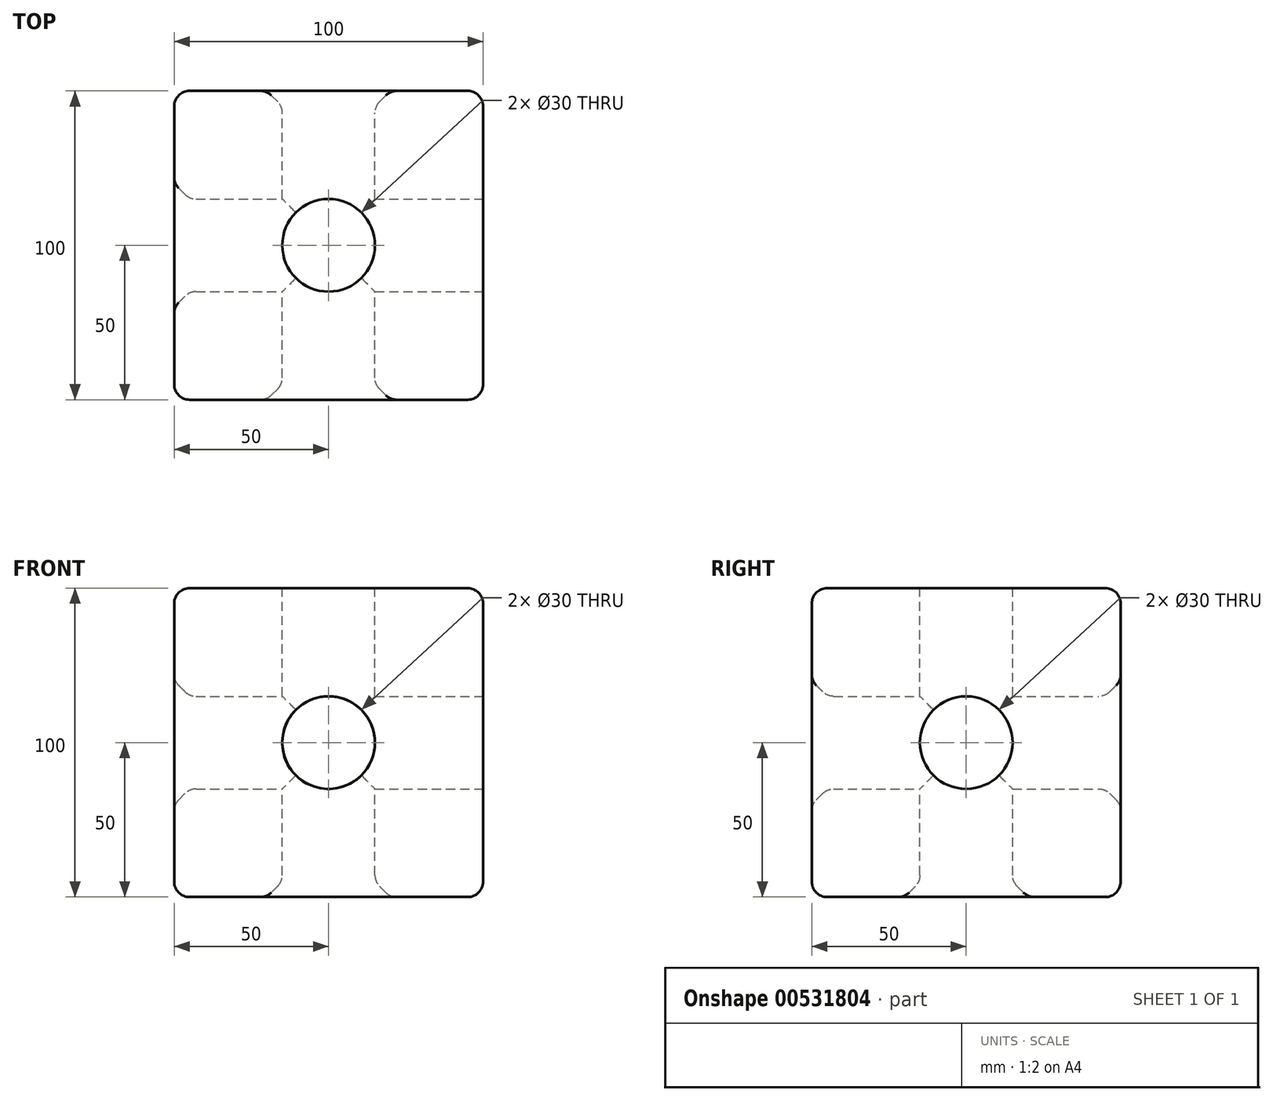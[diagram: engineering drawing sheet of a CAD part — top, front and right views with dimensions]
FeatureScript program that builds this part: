
annotation { "Feature Type Name" : "Feature", "Feature Type Description" : "" }
export const myFeature = defineFeature(function(context is Context, id is Id, definition is map)
    precondition{}
    {
        {
            var Q0;
            Q0=qCreatedBy(makeId("Front.planeOp"),FACE);
            var sketch = newSketch(context, id + "F0", { "sketchPlane" : qUnion([Q0])});
            skLineSegment(sketch, "E0.bottom", {"start": v(-50, 50) * mm, "end": v(50, 50) * mm});
            skLineSegment(sketch, "E0.top", {"start": v(-50, -50) * mm, "end": v(50, -50) * mm});
            skLineSegment(sketch, "E0.left", {"start": v(-50, 50) * mm, "end": v(-50, -50) * mm});
            skLineSegment(sketch, "E0.right", {"start": v(50, 50) * mm, "end": v(50, -50) * mm});
            skCircle(sketch, "E1", {"center": v(0, 0) * mm, "radius": 15 * mm});
            skSolve(sketch);
        }
        {
            var Q0;
            Q0=makeQuery(id+"F0.imprint","IMPRINT",FACE,{"disambiguationData":[TD([[makeQuery(id+"F0.imprint","IMPRINT",EDGE,{"derivedFrom":sQuery(id+"F0.wireOp",EDGE,"E0.bottom")}),-1.0]])]});
            extrude(context, id + "F1", {"entities" : qUnion([Q0]), "endBound" : BoundingType.SYMMETRIC, "depth" : 100 * mm, "offsetDistance" : 25 * mm});
        }
        {
            var Q0;
            Q0=makeQuery(id+"F1.opExtrude","SWEPT_FACE",FACE,{"disambiguationData":[OSD([sQuery(id+"F0.wireOp",EDGE,"E0.bottom")])]});
            var sketch = newSketch(context, id + "F2", { "sketchPlane" : qUnion([Q0])});
            skCircle(sketch, "E2", {"center": v(0, 0) * mm, "radius": 15 * mm});
            skSolve(sketch);
        }
        {
            var Q0;
            Q0 = qSketchRegion(id + "F2", true);
            extrude(context, id + "F3", {"entities" : qUnion([Q0]), "operationType" : NewBodyOperationType.REMOVE, "endBound" : BoundingType.THROUGH_ALL, "oppositeDirection" : true, "depth" : 25 * mm, "offsetDistance" : 25 * mm});
        }
        {
            var Q0;
            Q0=makeQuery(id+"F1.opExtrude","SWEPT_FACE",FACE,{"disambiguationData":[OSD([sQuery(id+"F0.wireOp",EDGE,"E0.right")])]});
            var sketch = newSketch(context, id + "F4", { "sketchPlane" : qUnion([Q0])});
            skCircle(sketch, "E3", {"center": v(0, 0) * mm, "radius": 15 * mm});
            skSolve(sketch);
        }
        {
            var Q0;
            Q0 = qSketchRegion(id + "F4", true);
            extrude(context, id + "F5", {"entities" : qUnion([Q0]), "operationType" : NewBodyOperationType.REMOVE, "endBound" : BoundingType.THROUGH_ALL, "oppositeDirection" : true, "depth" : 25 * mm, "offsetDistance" : 25 * mm});
        }
        {
            var Q0;
            Q0=makeQuery(id+"F1.opExtrude","CAP_EDGE",EDGE,{"disambiguationData":[OSD([sQuery(id+"F0.wireOp",EDGE,"E0.bottom")])],"isStart":true});
            var Q1;
            Q1=makeQuery(id+"F1.opExtrude","SWEPT_EDGE",EDGE,{"disambiguationData":[OSD([sQuery(id+"F0.wireOp",EDGE,"E0.bottom"),sQuery(id+"F0.wireOp",EDGE,"E0.left")])]});
            var Q2;
            Q2=makeQuery(id+"F1.opExtrude","CAP_EDGE",EDGE,{"disambiguationData":[OSD([sQuery(id+"F0.wireOp",EDGE,"E0.bottom")])],"isStart":false});
            var Q3;
            Q3=makeQuery(id+"F1.opExtrude","SWEPT_EDGE",EDGE,{"disambiguationData":[OSD([sQuery(id+"F0.wireOp",EDGE,"E0.bottom"),sQuery(id+"F0.wireOp",EDGE,"E0.right")])]});
            var Q4;
            Q4=makeQuery(id+"F1.opExtrude","CAP_EDGE",EDGE,{"disambiguationData":[OSD([sQuery(id+"F0.wireOp",EDGE,"E0.right")])],"isStart":true});
            var Q5;
            Q5=makeQuery(id+"F1.opExtrude","CAP_EDGE",EDGE,{"disambiguationData":[OSD([sQuery(id+"F0.wireOp",EDGE,"E0.left")])],"isStart":true});
            var Q6;
            Q6=makeQuery(id+"F1.opExtrude","CAP_EDGE",EDGE,{"disambiguationData":[OSD([sQuery(id+"F0.wireOp",EDGE,"E0.top")])],"isStart":true});
            var Q7;
            Q7=makeQuery(id+"F1.opExtrude","CAP_EDGE",EDGE,{"disambiguationData":[OSD([sQuery(id+"F0.wireOp",EDGE,"E0.right")])],"isStart":false});
            var Q8;
            Q8=makeQuery(id+"F1.opExtrude","SWEPT_EDGE",EDGE,{"disambiguationData":[OSD([sQuery(id+"F0.wireOp",EDGE,"E0.top"),sQuery(id+"F0.wireOp",EDGE,"E0.right")])]});
            var Q9;
            Q9=makeQuery(id+"F1.opExtrude","CAP_EDGE",EDGE,{"disambiguationData":[OSD([sQuery(id+"F0.wireOp",EDGE,"E0.top")])],"isStart":false});
            var Q10;
            Q10=makeQuery(id+"F1.opExtrude","CAP_EDGE",EDGE,{"disambiguationData":[OSD([sQuery(id+"F0.wireOp",EDGE,"E0.left")])],"isStart":false});
            var Q11;
            Q11=makeQuery(id+"F1.opExtrude","SWEPT_EDGE",EDGE,{"disambiguationData":[OSD([sQuery(id+"F0.wireOp",EDGE,"E0.top"),sQuery(id+"F0.wireOp",EDGE,"E0.left")])]});
            fillet(context, id + "F6", {"entities" : qUnion([Q0, Q1, Q2, Q3, Q4, Q5, Q6, Q7, Q8, Q9, Q10, Q11]), "radius" : 5 * mm, "tangentPropagation" : true, "allowEdgeOverflow" : false});
        }
        {
            var Q0;
            Q0=makeQuery(id+"F3.boolean.opBoolean","COPY",EDGE,{"derivedFrom":makeQuery(id+"F3.opExtrude","CAP_EDGE",EDGE,{"disambiguationData":[OSD([sQuery(id+"F2.wireOp",EDGE,"E2")])],"isStart":true})});
            var Q1;
            Q1=makeQuery(id+"F5.boolean.opBoolean","COPY",EDGE,{"derivedFrom":makeQuery(id+"F5.opExtrude","CAP_EDGE",EDGE,{"disambiguationData":[OSD([sQuery(id+"F4.wireOp",EDGE,"E3")])],"isStart":true})});
            var Q2;
            Q2=makeQuery(id+"F1.opExtrude","CAP_EDGE",EDGE,{"disambiguationData":[OSD([sQuery(id+"F0.wireOp",EDGE,"E1")])],"isStart":false});
            var Q3;
            Q3=makeQuery(id+"F3.boolean.opBoolean","INTERSECT",EDGE,{"derivedFrom":[makeQuery(id+"F1.opExtrude","SWEPT_FACE",FACE,{"disambiguationData":[OSD([sQuery(id+"F0.wireOp",EDGE,"E0.top")])]}),makeQuery(id+"F3.opExtrude","SWEPT_FACE",FACE,{"disambiguationData":[OSD([sQuery(id+"F2.wireOp",EDGE,"E2")])]})]});
            var Q4;
            Q4=makeQuery(id+"F5.boolean.opBoolean","INTERSECT",EDGE,{"derivedFrom":[makeQuery(id+"F1.opExtrude","SWEPT_FACE",FACE,{"disambiguationData":[OSD([sQuery(id+"F0.wireOp",EDGE,"E0.left")])]}),makeQuery(id+"F5.opExtrude","SWEPT_FACE",FACE,{"disambiguationData":[OSD([sQuery(id+"F4.wireOp",EDGE,"E3")])]})]});
            var Q5;
            Q5=makeQuery(id+"F1.opExtrude","CAP_EDGE",EDGE,{"disambiguationData":[OSD([sQuery(id+"F0.wireOp",EDGE,"E1")])],"isStart":true});
            chamfer(context, id + "F7", {"entities" : qUnion([Q0, Q1, Q2, Q3, Q4, Q5]), "width" : 5 * mm, "tangentPropagation" : true});
        }
        {
            var Q0;
            Q0=makeQuery(id+"F7.opChamfer","BLEND_EDGE",EDGE,{"blendedFrom":[makeQuery(id+"F3.boolean.opBoolean","COPY",EDGE,{"derivedFrom":makeQuery(id+"F3.opExtrude","CAP_EDGE",EDGE,{"disambiguationData":[OSD([sQuery(id+"F2.wireOp",EDGE,"E2")])],"isStart":true})}),makeQuery(id+"F1.opExtrude","SWEPT_FACE",FACE,{"disambiguationData":[OSD([sQuery(id+"F0.wireOp",EDGE,"E0.bottom")])]})],"blendedInto":[makeQuery(id+"F1.opExtrude","SWEPT_FACE",FACE,{"disambiguationData":[OSD([sQuery(id+"F0.wireOp",EDGE,"E0.bottom")])]})]});
            var Q1;
            Q1=makeQuery(id+"F7.opChamfer","BLEND_FACE",FACE,{"disambiguationData":[OSD([sQuery(id+"F2.wireOp",EDGE,"E2")])]});
            var Q2;
            {var subQ0=makeQuery(id+"F1.opExtrude","SWEPT_FACE",FACE,{"disambiguationData":[OSD([sQuery(id+"F0.wireOp",EDGE,"E0.left")])]});Q2=makeQuery(id+"F7.opChamfer","BLEND_EDGE",EDGE,{"blendedFrom":[makeQuery(id+"F5.boolean.opBoolean","INTERSECT",EDGE,{"derivedFrom":[subQ0,makeQuery(id+"F5.opExtrude","SWEPT_FACE",FACE,{"disambiguationData":[OSD([sQuery(id+"F4.wireOp",EDGE,"E3")])]})]}),subQ0],"blendedInto":[subQ0]});}
            var Q3;
            {var subQ0=makeQuery(id+"F1.opExtrude","SWEPT_FACE",FACE,{"disambiguationData":[OSD([sQuery(id+"F0.wireOp",EDGE,"E0.left")])]});var subQ3=makeQuery(id+"F5.opExtrude","SWEPT_FACE",FACE,{"disambiguationData":[OSD([sQuery(id+"F4.wireOp",EDGE,"E3")])]});Q3=makeQuery(id+"F7.opChamfer","BLEND_EDGE",EDGE,{"blendedFrom":[makeQuery(id+"F5.boolean.opBoolean","INTERSECT",EDGE,{"derivedFrom":[subQ0,subQ3]}),makeQuery(id+"F5.boolean.opBoolean","COPY",FACE,{"disambiguationData":[TD([subQ0])],"derivedFrom":subQ3})],"blendedInto":[makeQuery(id+"F5.boolean.opBoolean","COPY",FACE,{"disambiguationData":[TD([subQ0])],"derivedFrom":subQ3})]});}
            var Q4;
            {var subQ0=sQuery(id+"F0.wireOp",EDGE,"E1");var subQ1=makeQuery(id+"F1.opExtrude","SWEPT_FACE",FACE,{"disambiguationData":[OSD([subQ0])]});Q4=makeQuery(id+"F7.opChamfer","BLEND_EDGE",EDGE,{"blendedFrom":[makeQuery(id+"F1.opExtrude","CAP_EDGE",EDGE,{"disambiguationData":[OSD([subQ0])],"isStart":false}),makeQuery(id+"F3.boolean.opBoolean","SPLIT",FACE,{"disambiguationData":[TD([makeQuery(id+"F1.opExtrude","CAP_FACE",FACE,{"disambiguationData":[OSD([sQuery(id+"F0.wireOp",EDGE,"E0.bottom"),sQuery(id+"F0.wireOp",EDGE,"E0.top"),sQuery(id+"F0.wireOp",EDGE,"E0.left"),sQuery(id+"F0.wireOp",EDGE,"E0.right"),subQ0])],"isStart":false})])],"derivedFrom":subQ1})],"blendedInto":[makeQuery(id+"F3.boolean.opBoolean","SPLIT",FACE,{"disambiguationData":[TD([makeQuery(id+"F1.opExtrude","CAP_FACE",FACE,{"disambiguationData":[OSD([sQuery(id+"F0.wireOp",EDGE,"E0.bottom"),sQuery(id+"F0.wireOp",EDGE,"E0.top"),sQuery(id+"F0.wireOp",EDGE,"E0.left"),sQuery(id+"F0.wireOp",EDGE,"E0.right"),subQ0])],"isStart":false})])],"derivedFrom":subQ1})]});}
            var Q5;
            {var subQ0=sQuery(id+"F0.wireOp",EDGE,"E1");Q5=makeQuery(id+"F7.opChamfer","BLEND_EDGE",EDGE,{"blendedFrom":[makeQuery(id+"F1.opExtrude","CAP_EDGE",EDGE,{"disambiguationData":[OSD([subQ0])],"isStart":false}),makeQuery(id+"F1.opExtrude","CAP_FACE",FACE,{"disambiguationData":[OSD([sQuery(id+"F0.wireOp",EDGE,"E0.bottom"),sQuery(id+"F0.wireOp",EDGE,"E0.top"),sQuery(id+"F0.wireOp",EDGE,"E0.left"),sQuery(id+"F0.wireOp",EDGE,"E0.right"),subQ0])],"isStart":false})],"blendedInto":[makeQuery(id+"F1.opExtrude","CAP_FACE",FACE,{"disambiguationData":[OSD([sQuery(id+"F0.wireOp",EDGE,"E0.bottom"),sQuery(id+"F0.wireOp",EDGE,"E0.top"),sQuery(id+"F0.wireOp",EDGE,"E0.left"),sQuery(id+"F0.wireOp",EDGE,"E0.right"),subQ0])],"isStart":false})]});}
            var Q6;
            Q6=makeQuery(id+"F7.opChamfer","BLEND_EDGE",EDGE,{"blendedFrom":[makeQuery(id+"F5.boolean.opBoolean","COPY",EDGE,{"derivedFrom":makeQuery(id+"F5.opExtrude","CAP_EDGE",EDGE,{"disambiguationData":[OSD([sQuery(id+"F4.wireOp",EDGE,"E3")])],"isStart":true})}),makeQuery(id+"F1.opExtrude","SWEPT_FACE",FACE,{"disambiguationData":[OSD([sQuery(id+"F0.wireOp",EDGE,"E0.right")])]})],"blendedInto":[makeQuery(id+"F1.opExtrude","SWEPT_FACE",FACE,{"disambiguationData":[OSD([sQuery(id+"F0.wireOp",EDGE,"E0.right")])]})]});
            var Q7;
            {var subQ2=sQuery(id+"F4.wireOp",EDGE,"E3");Q7=makeQuery(id+"F7.opChamfer","BLEND_EDGE",EDGE,{"blendedFrom":[makeQuery(id+"F5.boolean.opBoolean","COPY",EDGE,{"derivedFrom":makeQuery(id+"F5.opExtrude","CAP_EDGE",EDGE,{"disambiguationData":[OSD([subQ2])],"isStart":true})}),makeQuery(id+"F5.boolean.opBoolean","COPY",FACE,{"disambiguationData":[TD([makeQuery(id+"F1.opExtrude","SWEPT_FACE",FACE,{"disambiguationData":[OSD([sQuery(id+"F0.wireOp",EDGE,"E0.right")])]})])],"derivedFrom":makeQuery(id+"F5.opExtrude","SWEPT_FACE",FACE,{"disambiguationData":[OSD([subQ2])]})})],"blendedInto":[makeQuery(id+"F5.boolean.opBoolean","COPY",FACE,{"disambiguationData":[TD([makeQuery(id+"F1.opExtrude","SWEPT_FACE",FACE,{"disambiguationData":[OSD([sQuery(id+"F0.wireOp",EDGE,"E0.right")])]})])],"derivedFrom":makeQuery(id+"F5.opExtrude","SWEPT_FACE",FACE,{"disambiguationData":[OSD([subQ2])]})})]});}
            var Q8;
            {var subQ0=sQuery(id+"F0.wireOp",EDGE,"E1");Q8=makeQuery(id+"F7.opChamfer","BLEND_EDGE",EDGE,{"blendedFrom":[makeQuery(id+"F1.opExtrude","CAP_EDGE",EDGE,{"disambiguationData":[OSD([subQ0])],"isStart":true}),makeQuery(id+"F1.opExtrude","CAP_FACE",FACE,{"disambiguationData":[OSD([sQuery(id+"F0.wireOp",EDGE,"E0.bottom"),sQuery(id+"F0.wireOp",EDGE,"E0.top"),sQuery(id+"F0.wireOp",EDGE,"E0.left"),sQuery(id+"F0.wireOp",EDGE,"E0.right"),subQ0])],"isStart":true})],"blendedInto":[makeQuery(id+"F1.opExtrude","CAP_FACE",FACE,{"disambiguationData":[OSD([sQuery(id+"F0.wireOp",EDGE,"E0.bottom"),sQuery(id+"F0.wireOp",EDGE,"E0.top"),sQuery(id+"F0.wireOp",EDGE,"E0.left"),sQuery(id+"F0.wireOp",EDGE,"E0.right"),subQ0])],"isStart":true})]});}
            var Q9;
            {var subQ0=sQuery(id+"F0.wireOp",EDGE,"E1");var subQ1=makeQuery(id+"F1.opExtrude","SWEPT_FACE",FACE,{"disambiguationData":[OSD([subQ0])]});Q9=makeQuery(id+"F7.opChamfer","BLEND_EDGE",EDGE,{"blendedFrom":[makeQuery(id+"F1.opExtrude","CAP_EDGE",EDGE,{"disambiguationData":[OSD([subQ0])],"isStart":true}),makeQuery(id+"F3.boolean.opBoolean","SPLIT",FACE,{"disambiguationData":[TD([makeQuery(id+"F1.opExtrude","CAP_FACE",FACE,{"disambiguationData":[OSD([sQuery(id+"F0.wireOp",EDGE,"E0.bottom"),sQuery(id+"F0.wireOp",EDGE,"E0.top"),sQuery(id+"F0.wireOp",EDGE,"E0.left"),sQuery(id+"F0.wireOp",EDGE,"E0.right"),subQ0])],"isStart":true})])],"derivedFrom":subQ1})],"blendedInto":[makeQuery(id+"F3.boolean.opBoolean","SPLIT",FACE,{"disambiguationData":[TD([makeQuery(id+"F1.opExtrude","CAP_FACE",FACE,{"disambiguationData":[OSD([sQuery(id+"F0.wireOp",EDGE,"E0.bottom"),sQuery(id+"F0.wireOp",EDGE,"E0.top"),sQuery(id+"F0.wireOp",EDGE,"E0.left"),sQuery(id+"F0.wireOp",EDGE,"E0.right"),subQ0])],"isStart":true})])],"derivedFrom":subQ1})]});}
            var Q10;
            {var subQ0=makeQuery(id+"F1.opExtrude","SWEPT_FACE",FACE,{"disambiguationData":[OSD([sQuery(id+"F0.wireOp",EDGE,"E0.top")])]});Q10=makeQuery(id+"F7.opChamfer","BLEND_EDGE",EDGE,{"blendedFrom":[makeQuery(id+"F3.boolean.opBoolean","INTERSECT",EDGE,{"derivedFrom":[subQ0,makeQuery(id+"F3.opExtrude","SWEPT_FACE",FACE,{"disambiguationData":[OSD([sQuery(id+"F2.wireOp",EDGE,"E2")])]})]}),subQ0],"blendedInto":[subQ0]});}
            var Q11;
            {var subQ0=makeQuery(id+"F1.opExtrude","SWEPT_FACE",FACE,{"disambiguationData":[OSD([sQuery(id+"F0.wireOp",EDGE,"E0.top")])]});var subQ1=makeQuery(id+"F3.opExtrude","SWEPT_FACE",FACE,{"disambiguationData":[OSD([sQuery(id+"F2.wireOp",EDGE,"E2")])]});Q11=makeQuery(id+"F7.opChamfer","BLEND_EDGE",EDGE,{"blendedFrom":[makeQuery(id+"F3.boolean.opBoolean","INTERSECT",EDGE,{"derivedFrom":[subQ0,subQ1]}),makeQuery(id+"F3.boolean.opBoolean","COPY",FACE,{"disambiguationData":[TD([subQ0])],"derivedFrom":subQ1})],"blendedInto":[makeQuery(id+"F3.boolean.opBoolean","COPY",FACE,{"disambiguationData":[TD([subQ0])],"derivedFrom":subQ1})]});}
            fillet(context, id + "F8", {"entities" : qUnion([Q0, Q1, Q2, Q3, Q4, Q5, Q6, Q7, Q8, Q9, Q10, Q11]), "radius" : 5 * mm, "tangentPropagation" : true, "allowEdgeOverflow" : false});
        }
    });
